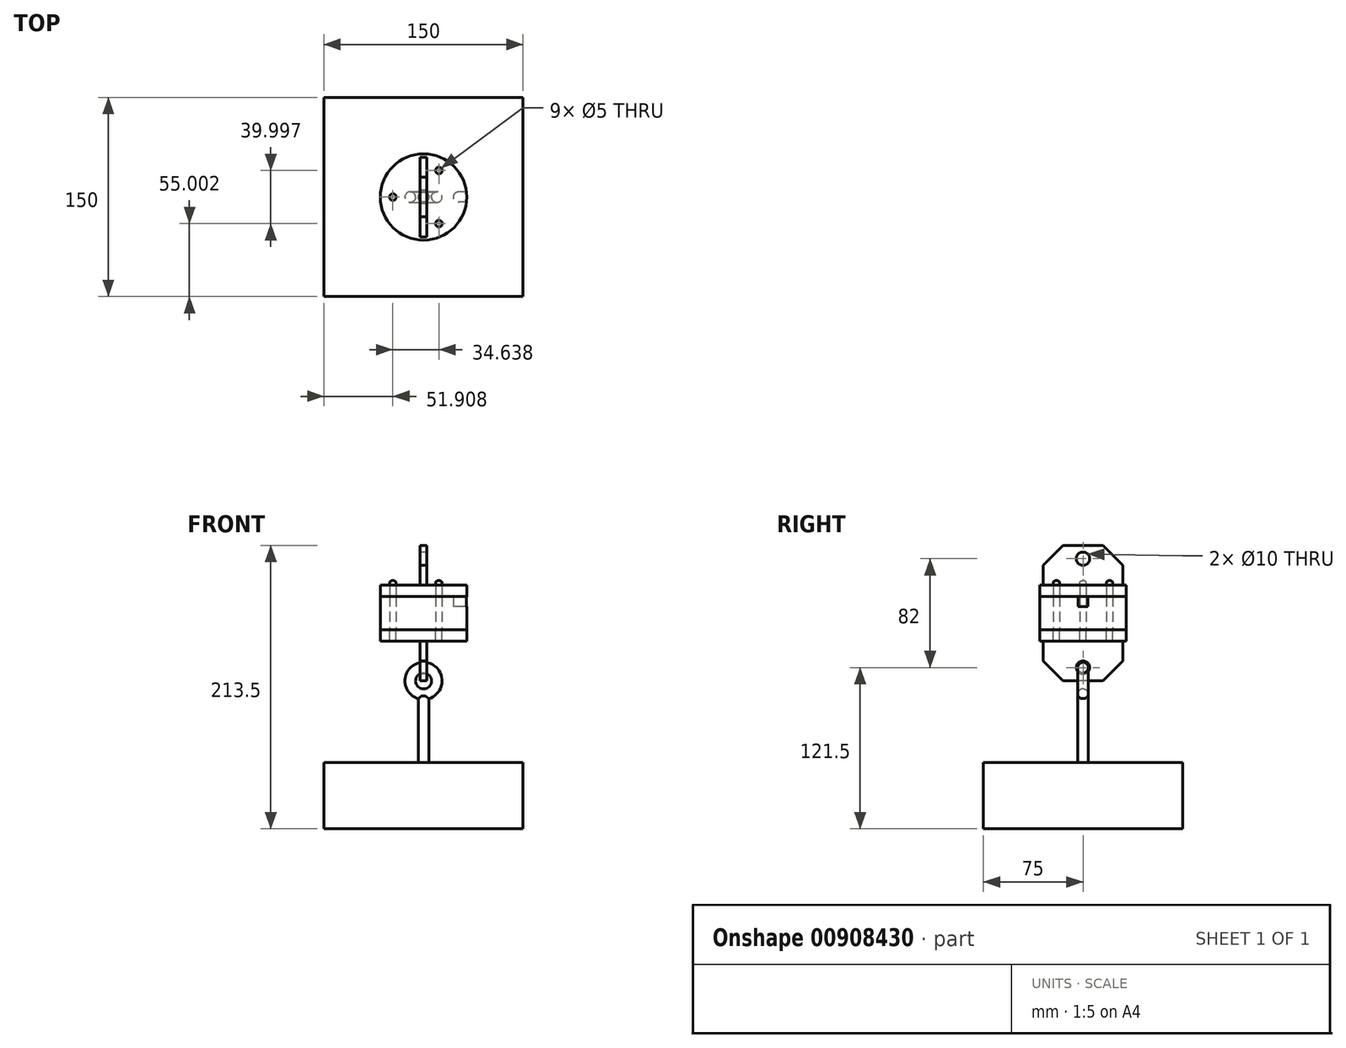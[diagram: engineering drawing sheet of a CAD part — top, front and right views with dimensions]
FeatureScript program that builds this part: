
annotation { "Feature Type Name" : "Feature", "Feature Type Description" : "" }
export const myFeature = defineFeature(function(context is Context, id is Id, definition is map)
    precondition{}
    {
        {
            var Q0;
            Q0=qCreatedBy(makeId("Top.planeOp"),FACE);
            var sketch = newSketch(context, id + "F0", { "sketchPlane" : qUnion([Q0])});
            skCircle(sketch, "E0", {"center": v(0, 0) * mm, "radius": 32.5 * mm});
            skLineSegment(sketch, "E1.bottom", {"start": v(75, -75) * mm, "end": v(-75, -75) * mm});
            skLineSegment(sketch, "E1.top", {"start": v(75, 75) * mm, "end": v(-75, 75) * mm});
            skLineSegment(sketch, "E1.left", {"start": v(75, -75) * mm, "end": v(75, 75) * mm});
            skLineSegment(sketch, "E1.right", {"start": v(-75, -75) * mm, "end": v(-75, 75) * mm});
            skCircle(sketch, "E2", {"center": v(-23.1, 0) * mm, "radius": 2.5 * mm});
            skCircle(sketch, "E3.1.0", {"center": v(11.55, -20) * mm, "radius": 2.5 * mm});
            skCircle(sketch, "E3.2.0", {"center": v(11.55, 20) * mm, "radius": 2.5 * mm});
            skLineSegment(sketch, "E4.bottom", {"start": v(38.86, -3.75) * mm, "end": v(26.14, -3.75) * mm});
            skLineSegment(sketch, "E4.top", {"start": v(38.86, 3.75) * mm, "end": v(26.14, 3.75) * mm});
            skLineSegment(sketch, "E4.left", {"start": v(38.86, -3.75) * mm, "end": v(38.86, 3.75) * mm});
            skLineSegment(sketch, "E4.right", {"start": v(26.14, -3.75) * mm, "end": v(26.14, 3.75) * mm});
            skPoint(sketch, "E4.middle", {"position": v(32.5, 0) * mm});
            skArc(sketch, "E5", {"start": v(26.14, 3.75) * mm, "mid": v(22.39, 0) * mm, "end": v(26.14, -3.75) * mm});
            skSolve(sketch);
        }
        {
            var Q0;
            Q0=makeQuery(id+"F0.imprint","IMPRINT",FACE,{"disambiguationData":[TD([[makeQuery(id+"F0.imprint","IMPRINT",EDGE,{"derivedFrom":sQuery(id+"F0.wireOp",EDGE,"E2")}),-1.0]])]});
            var Q1;
            Q1=makeQuery(id+"F0.imprint","IMPRINT",FACE,{"disambiguationData":[TD([[makeQuery(id+"F0.imprint","IMPRINT",EDGE,{"derivedFrom":sQuery(id+"F0.wireOp",EDGE,"E4.right")}),1.0]])]});
            var Q2;
            {var subQ6=sQuery(id+"F0.wireOp",EDGE,"E4.right");Q2=makeQuery(id+"F0.imprint","IMPRINT",FACE,{"disambiguationData":[TD([[makeQuery(id+"F0.imprint","IMPRINT",EDGE,{"derivedFrom":subQ6}),-1.0]])]});}
            extrude(context, id + "F1", {"entities" : qUnion([Q0, Q1, Q2]), "depth" : 25 * mm, "offsetDistance" : 25 * mm});
        }
        {
            var Q0;
            Q0=makeQuery(id+"F0.imprint","IMPRINT",FACE,{"disambiguationData":[TD([[makeQuery(id+"F0.imprint","IMPRINT",EDGE,{"derivedFrom":sQuery(id+"F0.wireOp",EDGE,"E2")}),-1.0]])]});
            var Q1;
            Q1=makeQuery(id+"F0.imprint","IMPRINT",FACE,{"disambiguationData":[TD([[makeQuery(id+"F0.imprint","IMPRINT",EDGE,{"derivedFrom":sQuery(id+"F0.wireOp",EDGE,"E4.right")}),1.0]])]});
            var Q2;
            {var subQ6=sQuery(id+"F0.wireOp",EDGE,"E4.right");Q2=makeQuery(id+"F0.imprint","IMPRINT",FACE,{"disambiguationData":[TD([[makeQuery(id+"F0.imprint","IMPRINT",EDGE,{"derivedFrom":subQ6}),-1.0]])]});}
            extrude(context, id + "F2", {"entities" : qUnion([Q0, Q1, Q2]), "depth" : 33.5 * mm, "offsetDistance" : 25 * mm, "hasSecondDirection" : true, "secondDirectionOppositeDirection" : false, "secondDirectionDepth" : 25 * mm});
        }
        {
            var Q0;
            Q0=makeQuery(id+"F0.imprint","IMPRINT",FACE,{"disambiguationData":[TD([[makeQuery(id+"F0.imprint","IMPRINT",EDGE,{"derivedFrom":sQuery(id+"F0.wireOp",EDGE,"E2")}),-1.0]])]});
            var Q1;
            {var subQ6=sQuery(id+"F0.wireOp",EDGE,"E4.right");Q1=makeQuery(id+"F0.imprint","IMPRINT",FACE,{"disambiguationData":[TD([[makeQuery(id+"F0.imprint","IMPRINT",EDGE,{"derivedFrom":subQ6}),-1.0]])]});}
            var Q2;
            Q2=makeQuery(id+"F0.imprint","IMPRINT",FACE,{"disambiguationData":[TD([[makeQuery(id+"F0.imprint","IMPRINT",EDGE,{"derivedFrom":sQuery(id+"F0.wireOp",EDGE,"E4.right")}),1.0]])]});
            extrude(context, id + "F3", {"entities" : qUnion([Q0, Q1, Q2]), "oppositeDirection" : true, "depth" : 8.5 * mm, "offsetDistance" : 25 * mm});
        }
        {
            var Q0;
            Q0=qCreatedBy(makeId("Right.planeOp"),FACE);
            var sketch = newSketch(context, id + "F4", { "sketchPlane" : qUnion([Q0])});
            skLineSegment(sketch, "E6.bottom", {"start": v(30, 33.5) * mm, "end": v(-30, 33.5) * mm});
            skLineSegment(sketch, "E6.top", {"start": v(30, 63.5) * mm, "end": v(-30, 63.5) * mm});
            skLineSegment(sketch, "E6.left", {"start": v(30, 33.5) * mm, "end": v(30, 63.5) * mm});
            skLineSegment(sketch, "E6.right", {"start": v(-30, 33.5) * mm, "end": v(-30, 63.5) * mm});
            skPoint(sketch, "E6.middle", {"position": v(0, 48.5) * mm});
            skLineSegment(sketch, "E7.bottom", {"start": v(30, -38.5) * mm, "end": v(-30, -38.5) * mm});
            skLineSegment(sketch, "E7.top", {"start": v(30, -8.5) * mm, "end": v(-30, -8.5) * mm});
            skLineSegment(sketch, "E7.left", {"start": v(30, -38.5) * mm, "end": v(30, -8.5) * mm});
            skLineSegment(sketch, "E7.right", {"start": v(-30, -38.5) * mm, "end": v(-30, -8.5) * mm});
            skPoint(sketch, "E7.middle", {"position": v(0, -23.5) * mm});
            skCircle(sketch, "E8", {"center": v(0, 53.5) * mm, "radius": 5 * mm});
            skCircle(sketch, "E9", {"center": v(0, -28.5) * mm, "radius": 5 * mm});
            skCircle(sketch, "E10", {"center": v(0, -28.5) * mm, "radius": 4 * mm});
            skSolve(sketch);
        }
        {
            var Q0;
            Q0=makeQuery(id+"F4.imprint","IMPRINT",FACE,{"disambiguationData":[TD([[makeQuery(id+"F4.imprint","IMPRINT",EDGE,{"derivedFrom":sQuery(id+"F4.wireOp",EDGE,"E6.bottom")}),-1.0]])]});
            var Q1;
            Q1=makeQuery(id+"F4.imprint","IMPRINT",FACE,{"disambiguationData":[TD([[makeQuery(id+"F4.imprint","IMPRINT",EDGE,{"derivedFrom":sQuery(id+"F4.wireOp",EDGE,"E7.bottom")}),-1.0]])]});
            extrude(context, id + "F5", {"entities" : qUnion([Q0, Q1]), "endBound" : BoundingType.SYMMETRIC, "depth" : 5 * mm, "offsetDistance" : 25 * mm});
        }
        {
            var Q0;
            Q0=makeQuery(id+"F5.opExtrude","SWEPT_EDGE",EDGE,{"disambiguationData":[OSD([sQuery(id+"F4.wireOp",EDGE,"E6.top"),sQuery(id+"F4.wireOp",EDGE,"E6.right")])]});
            var Q1;
            Q1=makeQuery(id+"F5.opExtrude","SWEPT_EDGE",EDGE,{"disambiguationData":[OSD([sQuery(id+"F4.wireOp",EDGE,"E6.top"),sQuery(id+"F4.wireOp",EDGE,"E6.left")])]});
            var Q2;
            Q2=makeQuery(id+"F5.opExtrude","SWEPT_EDGE",EDGE,{"disambiguationData":[OSD([sQuery(id+"F4.wireOp",EDGE,"E7.bottom"),sQuery(id+"F4.wireOp",EDGE,"E7.right")])]});
            var Q3;
            Q3=makeQuery(id+"F5.opExtrude","SWEPT_EDGE",EDGE,{"disambiguationData":[OSD([sQuery(id+"F4.wireOp",EDGE,"E7.bottom"),sQuery(id+"F4.wireOp",EDGE,"E7.left")])]});
            chamfer(context, id + "F6", {"entities" : qUnion([Q0, Q1, Q2, Q3]), "width" : 15 * mm, "tangentPropagation" : true});
        }
        {
            var Q0;
            Q0=makeQuery(id+"F0.imprint","IMPRINT",FACE,{"disambiguationData":[TD([[makeQuery(id+"F0.imprint","IMPRINT",EDGE,{"derivedFrom":sQuery(id+"F0.wireOp",EDGE,"E2")}),1.0]])]});
            var Q1;
            Q1=makeQuery(id+"F0.imprint","IMPRINT",FACE,{"disambiguationData":[TD([[makeQuery(id+"F0.imprint","IMPRINT",EDGE,{"derivedFrom":sQuery(id+"F0.wireOp",EDGE,"E3.2.0")}),1.0]])]});
            var Q2;
            Q2=makeQuery(id+"F0.imprint","IMPRINT",FACE,{"disambiguationData":[TD([[makeQuery(id+"F0.imprint","IMPRINT",EDGE,{"derivedFrom":sQuery(id+"F0.wireOp",EDGE,"E3.1.0")}),1.0]])]});
            extrude(context, id + "F7", {"entities" : qUnion([Q0, Q1, Q2]), "depth" : 37 * mm, "offsetDistance" : 25 * mm, "hasSecondDirection" : true, "secondDirectionOppositeDirection" : false, "secondDirectionDepth" : 33.5 * mm});
        }
        {
            var Q0;
            Q0=makeQuery(id+"F7.opExtrude","CAP_EDGE",EDGE,{"disambiguationData":[OSD([sQuery(id+"F0.wireOp",EDGE,"E2")])],"isStart":false});
            var Q1;
            Q1=makeQuery(id+"F7.opExtrude","CAP_EDGE",EDGE,{"disambiguationData":[OSD([sQuery(id+"F0.wireOp",EDGE,"E3.2.0")])],"isStart":false});
            var Q2;
            Q2=makeQuery(id+"F7.opExtrude","CAP_EDGE",EDGE,{"disambiguationData":[OSD([sQuery(id+"F0.wireOp",EDGE,"E3.1.0")])],"isStart":false});
            fillet(context, id + "F8", {"entities" : qUnion([Q0, Q1, Q2]), "radius" : 2 * mm, "tangentPropagation" : true, "allowEdgeOverflow" : false});
        }
        {
            var Q0;
            Q0=makeQuery(id+"F0.imprint","IMPRINT",FACE,{"disambiguationData":[TD([[makeQuery(id+"F0.imprint","IMPRINT",EDGE,{"derivedFrom":sQuery(id+"F0.wireOp",EDGE,"E4.right")}),1.0]])]});
            var Q1;
            {var subQ6=sQuery(id+"F0.wireOp",EDGE,"E4.right");Q1=makeQuery(id+"F0.imprint","IMPRINT",FACE,{"disambiguationData":[TD([[makeQuery(id+"F0.imprint","IMPRINT",EDGE,{"derivedFrom":subQ6}),-1.0]])]});}
            extrude(context, id + "F9", {"entities" : qUnion([Q0, Q1]), "operationType" : NewBodyOperationType.REMOVE, "depth" : 25 * mm, "offsetDistance" : 25 * mm, "hasSecondDirection" : true, "secondDirectionOppositeDirection" : false, "secondDirectionDepth" : 17.5 * mm});
        }
        {
            var Q0;
            Q0=makeQuery(id+"F0.imprint","IMPRINT",FACE,{"disambiguationData":[TD([[makeQuery(id+"F0.imprint","IMPRINT",EDGE,{"derivedFrom":sQuery(id+"F0.wireOp",EDGE,"E1.bottom")}),-1.0]])]});
            var Q1;
            Q1=makeQuery(id+"F0.imprint","IMPRINT",FACE,{"disambiguationData":[TD([[makeQuery(id+"F0.imprint","IMPRINT",EDGE,{"derivedFrom":sQuery(id+"F0.wireOp",EDGE,"E2")}),-1.0]])]});
            var Q2;
            Q2=makeQuery(id+"F0.imprint","IMPRINT",FACE,{"disambiguationData":[TD([[makeQuery(id+"F0.imprint","IMPRINT",EDGE,{"derivedFrom":sQuery(id+"F0.wireOp",EDGE,"E3.2.0")}),1.0]])]});
            var Q3;
            Q3=makeQuery(id+"F0.imprint","IMPRINT",FACE,{"disambiguationData":[TD([[makeQuery(id+"F0.imprint","IMPRINT",EDGE,{"derivedFrom":sQuery(id+"F0.wireOp",EDGE,"E2")}),1.0]])]});
            var Q4;
            Q4=makeQuery(id+"F0.imprint","IMPRINT",FACE,{"disambiguationData":[TD([[makeQuery(id+"F0.imprint","IMPRINT",EDGE,{"derivedFrom":sQuery(id+"F0.wireOp",EDGE,"E3.1.0")}),1.0]])]});
            var Q5;
            Q5=makeQuery(id+"F0.imprint","IMPRINT",FACE,{"disambiguationData":[TD([[makeQuery(id+"F0.imprint","IMPRINT",EDGE,{"derivedFrom":sQuery(id+"F0.wireOp",EDGE,"E4.right")}),1.0]])]});
            var Q6;
            {var subQ6=sQuery(id+"F0.wireOp",EDGE,"E4.right");Q6=makeQuery(id+"F0.imprint","IMPRINT",FACE,{"disambiguationData":[TD([[makeQuery(id+"F0.imprint","IMPRINT",EDGE,{"derivedFrom":subQ6}),-1.0]])]});}
            var Q7;
            {var subQ5=sQuery(id+"F0.wireOp",EDGE,"E4.left");Q7=makeQuery(id+"F0.imprint","IMPRINT",FACE,{"disambiguationData":[TD([[makeQuery(id+"F0.imprint","IMPRINT",EDGE,{"derivedFrom":subQ5}),1.0]])]});}
            extrude(context, id + "F10", {"entities" : qUnion([Q0, Q1, Q2, Q3, Q4, Q5, Q6, Q7]), "oppositeDirection" : true, "depth" : 150 * mm, "offsetDistance" : 25 * mm, "hasSecondDirection" : true, "secondDirectionOppositeDirection" : true, "secondDirectionDepth" : 100 * mm});
        }
        {
            var Q0;
            Q0=qCreatedBy(makeId("Front.planeOp"),FACE);
            var sketch = newSketch(context, id + "F11", { "sketchPlane" : qUnion([Q0])});
            skCircle(sketch, "E11", {"center": v(0, -38.5) * mm, "radius": 10 * mm});
            skSolve(sketch);
        }
        {
            var Q0;
            Q0=makeQuery(id+"F4.imprint","IMPRINT",FACE,{"disambiguationData":[TD([[makeQuery(id+"F4.imprint","IMPRINT",EDGE,{"derivedFrom":sQuery(id+"F4.wireOp",EDGE,"E10")}),1.0]])]});
            var Q1;
            Q1=sQuery(id+"F11.wireOp",EDGE,"E11");
            revolve(context, id + "F12", {"surfaceOperationType" : NewSurfaceOperationType.NEW, "entities" : qUnion([Q0]), "axis" : qUnion([Q1]), "revolveType" : RevolveType.FULL});
        }
        {
            var Q0;
            Q0=makeQuery(id+"F0.imprint","IMPRINT",FACE,{"disambiguationData":[TD([[makeQuery(id+"F0.imprint","IMPRINT",EDGE,{"derivedFrom":sQuery(id+"F0.wireOp",EDGE,"E1.bottom")}),-1.0]])]});
            var sketch = newSketch(context, id + "F13", { "sketchPlane" : qUnion([Q0])});
            skCircle(sketch, "E12", {"center": v(0, 0) * mm, "radius": 4 * mm});
            skSolve(sketch);
        }
        {
            var Q0;
            Q0=makeQuery(id+"F13.imprint","IMPRINT",FACE,{"disambiguationData":[TD([[makeQuery(id+"F13.imprint","IMPRINT",EDGE,{"derivedFrom":sQuery(id+"F13.wireOp",EDGE,"E12")}),1.0]])]});
            extrude(context, id + "F14", {"entities" : qUnion([Q0]), "operationType" : NewBodyOperationType.ADD, "oppositeDirection" : true, "depth" : 100 * mm, "offsetDistance" : 25 * mm, "hasSecondDirection" : true, "secondDirectionOppositeDirection" : true, "secondDirectionDepth" : 50 * mm});
        }
    });
